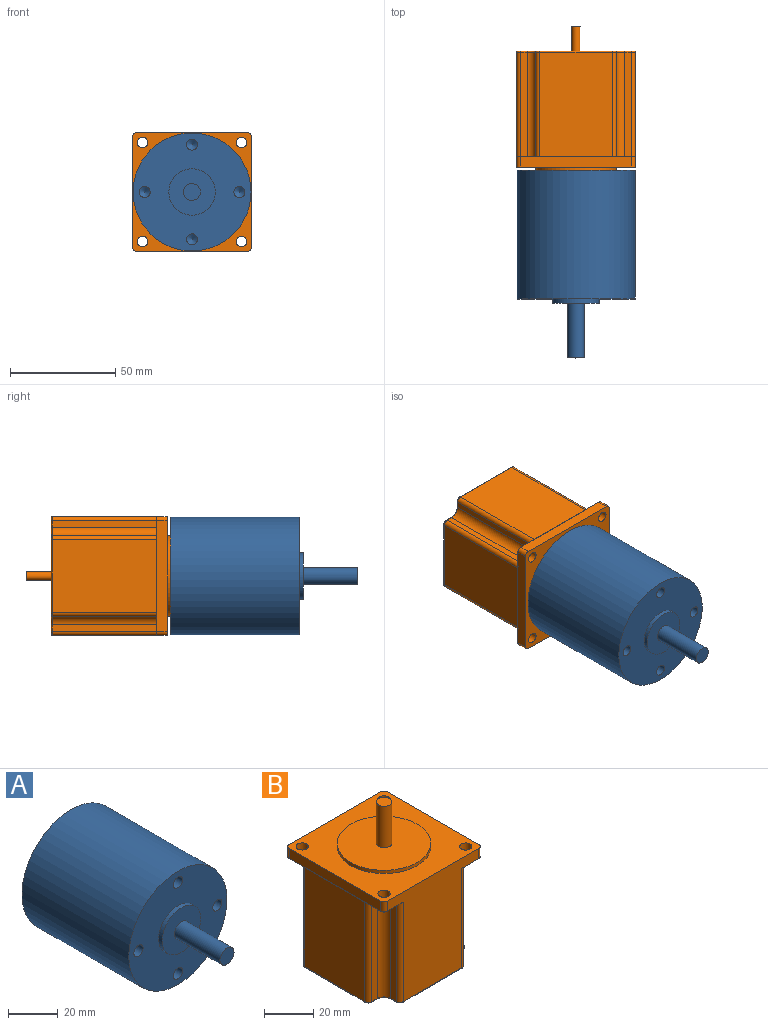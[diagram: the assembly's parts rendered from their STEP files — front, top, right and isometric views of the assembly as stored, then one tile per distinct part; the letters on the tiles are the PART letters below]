
ASSEMBLY  parts=2 mates=1
PART A: 15 faces, bbox 56x89x56 mm
  f0: cylinder r=28mm len=61mm, axis (0,1,0), area 10731.7mm2, adj f1,f2
  f1: plane 56x56mm, normal (0,-1,0), area 1996.3mm2, adj f0,f3,f7,f9,f11,f13
  f2: plane 56x56mm, normal (0,1,0), area 2463mm2, adj f0
  f3: cylinder r=11mm len=22mm, axis (0,1,0), area 138.2mm2, adj f1,f4
  f4: plane 22x22mm, normal (0,-1,0), area 329.9mm2, adj f3,f5
  f5: cylinder r=4mm len=26mm, axis (0,1,0), area 653.5mm2, adj f4,f6
  f6: plane 8x8mm, normal (0,-1,0), area 50.3mm2, adj f5
  f7: cylinder r=2.62mm len=12.7mm, axis (0,-1,0), area 209.5mm2, adj f1,f8
  f8: cone r=0mm half-angle=59deg, axis (0,-1,0), area 25.3mm2, adj f7
  f9: cylinder r=2.62mm len=12.7mm, axis (0,-1,0), area 209.5mm2, adj f1,f10
  f10: cone r=0mm half-angle=59deg, axis (0,-1,0), area 25.3mm2, adj f9
  f11: cylinder r=2.62mm len=12.7mm, axis (0,-1,0), area 209.5mm2, adj f1,f12
  f12: cone r=0mm half-angle=59deg, axis (0,-1,0), area 25.3mm2, adj f11
  f13: cylinder r=2.62mm len=12.7mm, axis (0,-1,0), area 209.5mm2, adj f1,f14
  f14: cone r=0mm half-angle=59deg, axis (0,-1,0), area 25.3mm2, adj f13
PART B: 74 faces, bbox 56.7x56.7x89.2 mm
  f0: cylinder r=0.61mm len=3mm, axis (0,0,1), area 11.5mm2, adj f1,f42
  f1: plane 1.22x1.22mm, normal (0,0,-1), area 1.2mm2, adj f0
  f2: cylinder r=0.61mm len=3mm, axis (0,0,1), area 11.5mm2, adj f3,f42
  f3: plane 1.22x1.22mm, normal (0,0,-1), area 1.2mm2, adj f2
  f4: cylinder r=2mm len=12mm, axis (0,0,-1), area 150.8mm2, adj f5,f42
  f5: plane 4x4mm, normal (0,0,-1), area 12.6mm2, adj f4
  f6: cylinder r=0.5mm len=3mm, axis (0,-1,0), area 2.4mm2, adj f7,f8,f41,f42
  f7: torus R=1.5mm, axis (0,0,1), area 2.2mm2, adj f6,f9,f40,f42
  f8: torus R=4.5mm, axis (0,0,1), area 5.2mm2, adj f6,f10,f42,f73
  f9: cylinder r=0.5mm len=34.4mm, axis (-1,0,0), area 27mm2, adj f7,f11,f39,f42
  f10: cylinder r=0.5mm len=3mm, axis (-1,0,0), area 2.4mm2, adj f8,f12,f42,f72
  f11: torus R=1.5mm, axis (0,0,1), area 2.2mm2, adj f9,f13,f38,f42
  f12: torus R=1.5mm, axis (0,0,1), area 2.2mm2, adj f10,f14,f42,f71
  f13: cylinder r=0.5mm len=3mm, axis (0,1,0), area 2.4mm2, adj f11,f15,f37,f42
  f14: cylinder r=0.5mm len=34.4mm, axis (0,-1,0), area 27mm2, adj f12,f16,f42,f70
  f15: torus R=4.5mm, axis (0,0,1), area 5.2mm2, adj f13,f17,f36,f42
  f16: torus R=1.5mm, axis (0,0,1), area 2.2mm2, adj f14,f18,f42,f69
  f17: cylinder r=0.5mm len=3mm, axis (-1,0,0), area 2.4mm2, adj f15,f19,f35,f42
  f18: cylinder r=0.5mm len=3mm, axis (1,0,0), area 2.4mm2, adj f16,f20,f42,f68
  f19: torus R=1.5mm, axis (0,0,1), area 2.2mm2, adj f17,f21,f34,f42
  f20: torus R=4.5mm, axis (0,0,1), area 5.2mm2, adj f18,f22,f42,f67
  f21: cylinder r=0.5mm len=34.4mm, axis (0,1,0), area 27mm2, adj f19,f23,f33,f42
  f22: cylinder r=0.5mm len=3mm, axis (0,-1,0), area 2.4mm2, adj f20,f24,f42,f66
  f23: torus R=1.5mm, axis (0,0,1), area 2.2mm2, adj f21,f25,f32,f42
  f24: torus R=1.5mm, axis (0,0,1), area 2.2mm2, adj f22,f26,f42,f65
  f25: cylinder r=0.5mm len=3.62mm, axis (1,0,0), area 2.8mm2, adj f23,f27,f31,f42
  f26: cylinder r=0.5mm len=33.78mm, axis (1,0,0), area 26.5mm2, adj f24,f28,f42,f55
  f27: torus R=4.5mm, axis (0,0,1), area 5.2mm2, adj f25,f29,f30,f42
  f28: torus R=1.5mm, axis (0,0,1), area 2.2mm2, adj f26,f29,f42,f64
  f29: cylinder r=0.5mm len=3mm, axis (0,1,0), area 2.4mm2, adj f27,f28,f42,f63
  f30: cylinder r=4mm len=49.5mm, axis (0,0,1), area 311mm2, adj f27,f31,f61,f63
  f31: plane 49.5x3.62mm, normal (0,-1,0), area 179mm2, adj f25,f30,f32,f61
  f32: cylinder r=2mm len=49.5mm, axis (0,0,1), area 155.5mm2, adj f23,f31,f33,f61
  f33: plane 54.5x52.42mm, normal (1,0,0), area 1964.9mm2, adj f21,f32,f34,f51,f53,f54,f56,f61
  f34: cylinder r=2mm len=49.5mm, axis (0,0,1), area 155.5mm2, adj f19,f33,f35,f53
  f35: plane 49.5x3mm, normal (0,1,0), area 148.5mm2, adj f17,f34,f36,f53
  f36: cylinder r=4mm len=49.5mm, axis (0,0,1), area 311mm2, adj f15,f35,f37,f53
  f37: plane 49.5x3mm, normal (1,0,0), area 148.5mm2, adj f13,f36,f38,f53
  f38: cylinder r=2mm len=49.5mm, axis (0,0,1), area 155.5mm2, adj f11,f37,f39,f53
  f39: plane 49.5x34.4mm, normal (0,1,0), area 1702.8mm2, adj f9,f38,f40,f53
  f40: cylinder r=2mm len=49.5mm, axis (0,0,1), area 155.5mm2, adj f7,f39,f41,f53
  f41: plane 49.5x3mm, normal (-1,0,0), area 148.5mm2, adj f6,f40,f53,f73
  f42: plane 55.4x55.4mm, normal (0,0,-1), area 2738.2mm2, adj f0,f2,f4,f6,f7,f8,f9,f10
  f43: cylinder r=2.5mm len=5mm, axis (0,0,-1), area 78.5mm2, adj f56,f58
  f44: cylinder r=2.5mm len=5mm, axis (0,0,-1), area 78.5mm2, adj f56,f61
  f45: cylinder r=2.5mm len=5mm, axis (0,0,-1), area 78.5mm2, adj f53,f56
  f46: cylinder r=2.5mm len=5mm, axis (0,0,-1), area 78.5mm2, adj f53,f56
  f47: cylinder r=3.17mm len=20.6mm, axis (0,0,1), area 411mm2, adj f48,f50
  f48: plane 6.35x6.35mm, normal (0,0,1), area 31.7mm2, adj f47
  f49: cylinder r=19.05mm len=38.1mm, axis (0,0,1), area 191.5mm2, adj f50,f56
  f50: plane 38.1x38.1mm, normal (0,0,1), area 1108.4mm2, adj f47,f49
  f51: cylinder r=2mm len=5mm, axis (0,0,1), area 15.7mm2, adj f33,f52,f53,f56
  f52: plane 52.38x5mm, normal (0,1,0), area 261.9mm2, adj f51,f53,f56,f60
  f53: plane 56.38x11.02mm, normal (0,0,-1), area 118.5mm2, adj f33,f34,f35,f36,f37,f38,f39,f40
  f54: cylinder r=2mm len=5mm, axis (0,0,1), area 15.7mm2, adj f33,f55,f56,f61
  f55: plane 54.5x52.38mm, normal (0,-1,0), area 1934.2mm2, adj f26,f54,f56,f57,f58,f61,f64,f65
  f56: plane 56.42x56.38mm, normal (0,0,1), area 1958.9mm2, adj f33,f43,f44,f45,f46,f49,f51,f52
  f57: cylinder r=2mm len=5mm, axis (0,0,1), area 15.7mm2, adj f55,f56,f58,f59
  f58: plane 10.98x10.72mm, normal (0,0,-1), area 58.6mm2, adj f43,f55,f57,f59,f65,f66,f67,f68
  f59: plane 52.42x5mm, normal (-1,0,0), area 262.1mm2, adj f53,f56,f57,f58,f60,f62
  f60: cylinder r=2mm len=5mm, axis (0,0,1), area 15.7mm2, adj f52,f53,f56,f59
  f61: plane 11.62x11mm, normal (0,0,-1), area 64.3mm2, adj f30,f31,f32,f33,f44,f54,f55,f63
  f62: plane 34.96x0.02mm, normal (0,0,1), area 0.7mm2, adj f59,f69,f70,f71
  f63: plane 49.5x3mm, normal (1,0,0), area 148.5mm2, adj f29,f30,f61,f64
  f64: cylinder r=2mm len=49.5mm, axis (0,0,1), area 155.5mm2, adj f28,f55,f61,f63
  f65: cylinder r=2mm len=49.5mm, axis (0,0,1), area 155.5mm2, adj f24,f55,f58,f66
  f66: plane 49.5x3mm, normal (-1,0,0), area 148.5mm2, adj f22,f58,f65,f67
  f67: cylinder r=4mm len=49.5mm, axis (0,0,1), area 311mm2, adj f20,f58,f66,f68
  f68: plane 49.5x3mm, normal (0,-1,0), area 148.5mm2, adj f18,f58,f67,f69
  f69: cylinder r=2mm len=49.5mm, axis (0,0,1), area 155.5mm2, adj f16,f58,f62,f68,f70
  f70: plane 49.5x34.4mm, normal (-1,0,0), area 1702.8mm2, adj f14,f62,f69,f71
  f71: cylinder r=2mm len=49.5mm, axis (0,0,1), area 155.5mm2, adj f12,f53,f62,f70,f72
  f72: plane 49.5x3mm, normal (0,1,0), area 148.5mm2, adj f10,f53,f71,f73
  f73: cylinder r=4mm len=49.5mm, axis (0,0,1), area 311mm2, adj f8,f41,f53,f72
PLACE A t=(0,-30.5,0)mm
PLACE B rot(axis=(1,0,0),90deg) t=(28.19,56.6,-28.21)mm
MATE fastened B.f47 <-> A.f0  axis (0,-1,0) through (0,0,0)mm
